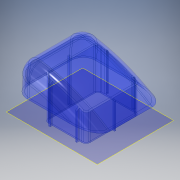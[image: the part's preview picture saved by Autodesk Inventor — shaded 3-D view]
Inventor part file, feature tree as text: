
AUTODESK INVENTOR PART (.ipt)
format: ipt  version: 2017 (Build 210142000, 142)  size: 427,008 bytes
history: native  units: in
note: dims shown in document units (in); Inventor stores cm internally (conversion verified against a paired STEP export)
features: extrude x2, sketch x2, fillet x1, shell x1, plane x1, projected_geometry x1
ambient origin geometry x8: Origin, YZ Plane, XZ Plane, XY Plane, X Axis, Y Axis, Z Axis, Center Point
bodies: Solid1 (feature_tree)
feature tree (8):
  extrude  "Extrusion1"  Depth=6.0in
  fillet  "Fillet1"  Radius=6.0in
  shell  "Shell1"  Thickness=0.64in
  plane  "Work Plane2"
  extrude  "Extrusion2"  Depth=0.4in
  sketch  "Sketch1"  dims[d0=3.04in d2=6.0in d6=6.0in d9=0.64in]
  sketch  "Sketch3"  dims[d10=3.01in d11=0.4in d12=2.55in d13=0.0in d14=0.5in d15=0.07in d36=0.67in d37=1.97in d38=0.68in d39=1.54in d40=0.29in d41=0.15in d42=0.05in d43=0.95in d44=1.94in d45=1.28in d46=0.09in d47=0.05in d48=0.025in d49=0.09in d50=0.05in d51=0.025in d52=0.09in d53=0.05in d54=0.025in d55=0.09in d56=0.025in d57=0.09in d58=0.05in d59=0.025in d60=0.09in d61=0.05in d62=0.025in d63=3.0in d64=0.0in]
  projected_geometry  "Projected Loop4"
